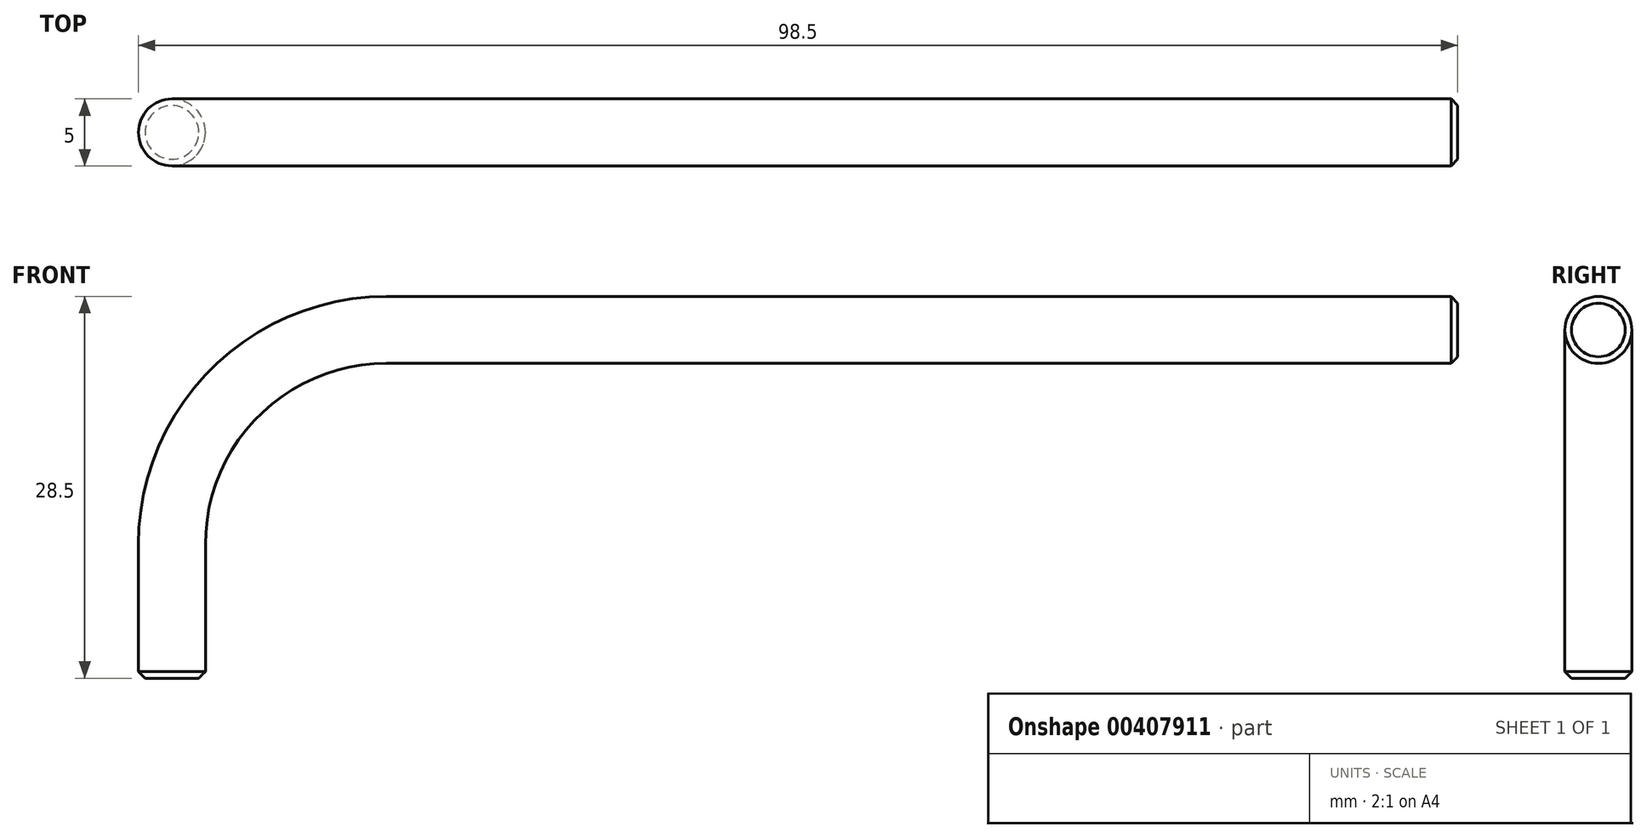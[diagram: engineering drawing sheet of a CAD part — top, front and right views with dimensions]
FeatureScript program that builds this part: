
annotation { "Feature Type Name" : "Feature", "Feature Type Description" : "" }
export const myFeature = defineFeature(function(context is Context, id is Id, definition is map)
    precondition{}
    {
        {
            var Q0;
            Q0=qCreatedBy(makeId("Front.planeOp"),FACE);
            var sketch = newSketch(context, id + "F0", { "sketchPlane" : qUnion([Q0])});
            skLineSegment(sketch, "E0", {"start": v(0, 0) * mm, "end": v(-80, 0) * mm});
            skArc(sketch, "E1", {"start": v(-80, 0) * mm, "mid": v(-91.31, -4.69) * mm, "end": v(-96, -16) * mm});
            skLineSegment(sketch, "E2", {"start": v(-96, -16) * mm, "end": v(-96, -26) * mm});
            skSolve(sketch);
        }
        {
            var Q0;
            Q0=qCreatedBy(makeId("Right.planeOp"),FACE);
            var sketch = newSketch(context, id + "F1", { "sketchPlane" : qUnion([Q0])});
            skCircle(sketch, "E3", {"center": v(0, 0) * mm, "radius": 2.5 * mm});
            skSolve(sketch);
        }
        {
            var Q0;
            Q0=makeQuery(id+"F1.imprint","IMPRINT",FACE,{"disambiguationData":[TD([[makeQuery(id+"F1.imprint","IMPRINT",EDGE,{"derivedFrom":sQuery(id+"F1.wireOp",EDGE,"E3")}),1.0]])]});
            var Q1;
            Q1=sQuery(id+"F0.wireOp",EDGE,"E0");
            var Q2;
            Q2=sQuery(id+"F0.wireOp",EDGE,"E1");
            var Q3;
            Q3=sQuery(id+"F0.wireOp",EDGE,"E2");
            sweep(context, id + "F2", {"profiles" : qUnion([Q0]), "path" : qUnion([Q1, Q2, Q3])});
        }
        {
            var Q0;
            Q0=makeQuery(id+"F2.opSweep","CAP_EDGE",EDGE,{"disambiguationData":[OSD([sQuery(id+"F0.wireOp",VERTEX,"E2.end"),sQuery(id+"F1.wireOp",EDGE,"E3")])],"isStart":false});
            var Q1;
            Q1=makeQuery(id+"F2.opSweep","CAP_EDGE",EDGE,{"disambiguationData":[OSD([sQuery(id+"F0.wireOp",VERTEX,"E0.start"),sQuery(id+"F1.wireOp",EDGE,"E3")])],"isStart":true});
            chamfer(context, id + "F3", {"entities" : qUnion([Q0, Q1]), "width" : 0.5 * mm, "tangentPropagation" : true});
        }
    });
